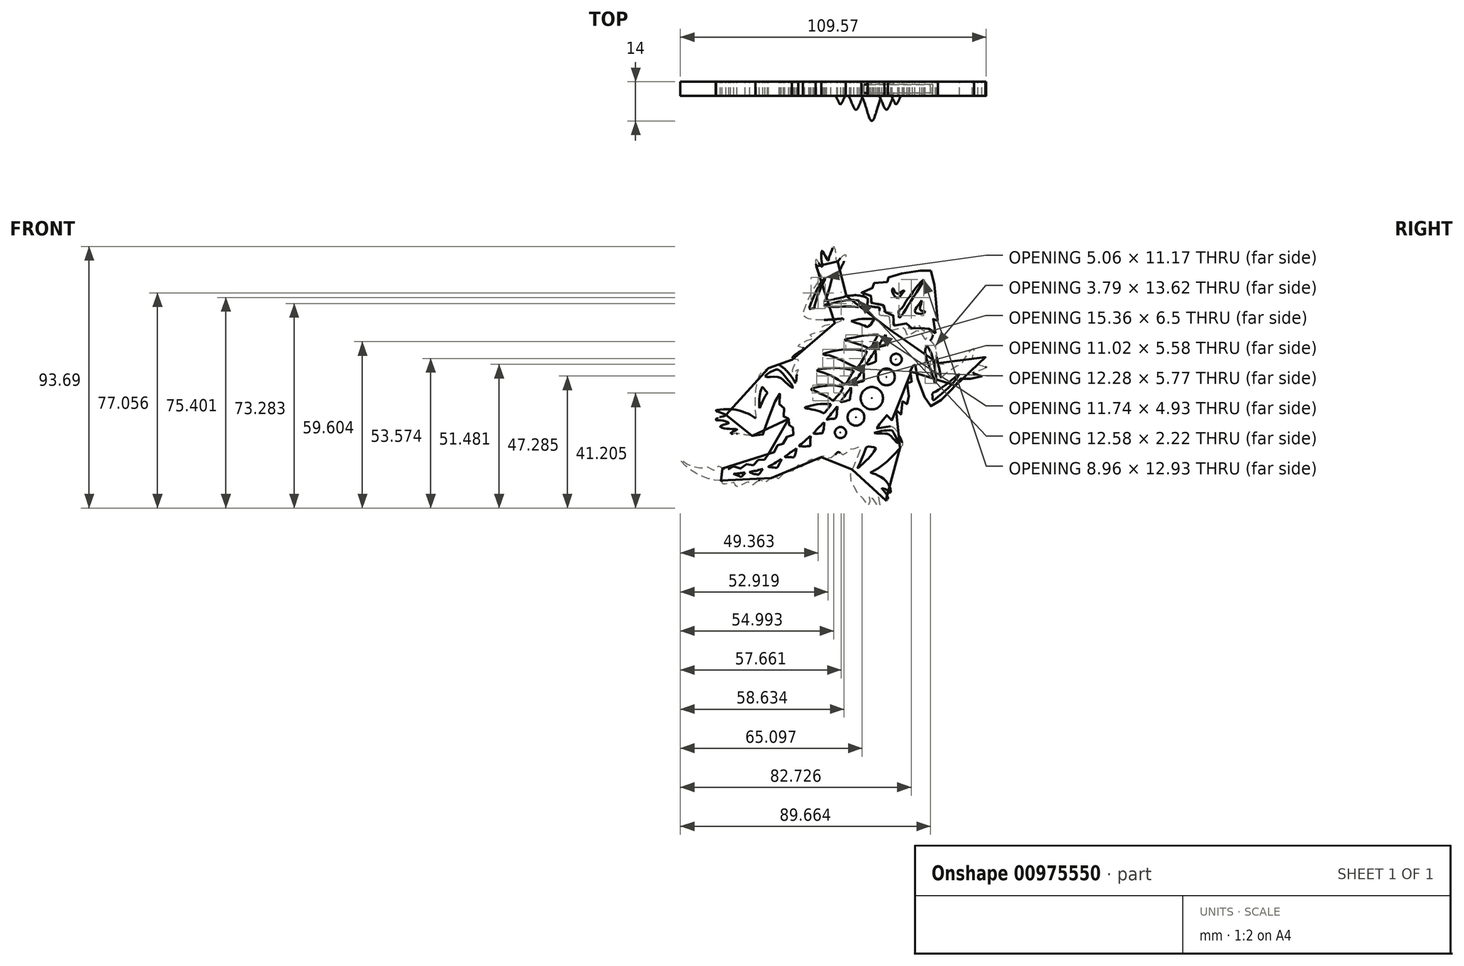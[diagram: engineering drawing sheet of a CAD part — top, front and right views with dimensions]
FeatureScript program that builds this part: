
annotation { "Feature Type Name" : "Feature", "Feature Type Description" : "" }
export const myFeature = defineFeature(function(context is Context, id is Id, definition is map)
    precondition{}
    {
        {
            var Q0;
            Q0=qCreatedBy(makeId("Front.planeOp"),FACE);
            var sketch = newSketch(context, id + "F0", { "sketchPlane" : qUnion([Q0])});
            skFitSpline(sketch, "E0", {"points": [v(30.98, 38.07) * mm, v(31.77, 36.1) * mm, v(32.57, 30.36) * mm, v(33.16, 24.69) * mm, v(33.49, 20.2) * mm, v(32.73, 21.01) * mm, v(31.9, 21.39) * mm, v(32.1, 19.86) * mm, v(32.63, 16.77) * mm, v(32.17, 14.46) * mm, v(30.12, 17.43) * mm, v(29.13, 16.1) * mm, v(27.08, 18.28) * mm, v(26.59, 18.68) * mm, v(24.12, 17.21) * mm, v(23.4, 17.05) * mm, v(22.34, 19.03) * mm, v(21.8, 19.22) * mm, v(18.26, 18.5) * mm, v(17.54, 18.54) * mm, v(17.59, 20.46) * mm, v(17.38, 22.76) * mm, v(16.26, 23.16) * mm, v(14.34, 23.28) * mm, v(13.92, 23.44) * mm, v(14, 25.28) * mm, v(14.04, 25.87) * mm, v(10.42, 26.54) * mm, v(9.56, 26.64) * mm, v(9.6, 27.95) * mm, v(9.65, 28.97) * mm, v(7.14, 29.74) * mm, v(6.18, 29.96) * mm, v(7.76, 31.22) * mm, v(10.13, 31.88) * mm, v(8.42, 32.8) * mm, v(12.25, 33.84) * mm, v(15.61, 33.83) * mm, v(14.75, 34.36) * mm, v(14.38, 34.8) * mm, v(15.66, 35.53) * mm, v(17.25, 36.18) * mm, v(21.91, 37.35) * mm, v(27.53, 38.14) * mm, v(29.94, 38.54) * mm, v(30.98, 38.07) * mm]});
            skFitSpline(sketch, "E1", {"points": [v(19.45, 29.85) * mm, v(20.35, 30.4) * mm, v(21.46, 30.98) * mm, v(21.33, 30.6) * mm, v(20.9, 30.12) * mm, v(20.16, 29.02) * mm, v(19.1, 28.32) * mm, v(17.88, 29.2) * mm, v(17.25, 30.44) * mm, v(17.21, 31.24) * mm, v(17.48, 31.8) * mm, v(18.04, 30.71) * mm, v(18.74, 30) * mm, v(19.45, 29.85) * mm]});
            skFitSpline(sketch, "E2", {"points": [v(27.77, 27.41) * mm, v(27.7, 26.6) * mm, v(27.26, 25.37) * mm, v(27.1, 24.63) * mm, v(27.46, 23.88) * mm, v(28.57, 23.55) * mm, v(29, 23.37) * mm, v(28.56, 22.98) * mm, v(27.22, 22.63) * mm, v(25.83, 22.88) * mm, v(25.3, 23.53) * mm, v(25.85, 24.77) * mm, v(26.88, 26.2) * mm, v(27.77, 27.41) * mm]});
            skFitSpline(sketch, "E3", {"points": [v(28.5, 34.9) * mm, v(27.24, 32.43) * mm, v(24.96, 28.8) * mm, v(22.63, 25.34) * mm, v(21.6, 23.47) * mm, v(19.69, 21.14) * mm, v(19.69, 21.84) * mm, v(19.55, 22.77) * mm, v(19.5, 23.7) * mm, v(20.2, 24.22) * mm, v(21.04, 25.06) * mm, v(22.35, 27.49) * mm, v(23.6, 28.93) * mm, v(25.66, 31.92) * mm, v(26.6, 33) * mm, v(28.5, 34.9) * mm]});
            skFitSpline(sketch, "E4", {"points": [v(16.5, 16.87) * mm, v(17.44, 16.9) * mm, v(19.63, 17.39) * mm, v(21.31, 17.57) * mm, v(21.73, 16.94) * mm, v(22.25, 15.64) * mm, v(22.65, 15.04) * mm, v(23.64, 15.34) * mm, v(25.2, 16.21) * mm, v(26.14, 16.7) * mm, v(27.05, 16.05) * mm, v(27.92, 15.1) * mm, v(29.16, 13.48) * mm, v(29.47, 13.82) * mm, v(29.68, 14.15) * mm, v(31.3, 12.65) * mm, v(32.54, 10.76) * mm, v(33.07, 7.62) * mm, v(34.14, 2.7) * mm, v(34.44, 1.05) * mm, v(34.67, -0.18) * mm, v(35.23, 0.28) * mm, v(37.82, 2.37) * mm, v(41.03, 4.33) * mm, v(42.2, 4.96) * mm, v(43.62, 7.27) * mm, v(45.23, 9.43) * mm, v(46.45, 10.27) * mm, v(46.36, 9.2) * mm, v(45.96, 7.32) * mm, v(45.9, 6.76) * mm, v(46.93, 6.79) * mm, v(49.42, 7.22) * mm, v(50.64, 7.17) * mm, v(49.98, 6.44) * mm, v(48.25, 4.94) * mm, v(47.94, 4.51) * mm, v(48.93, 4.14) * mm, v(50.4, 3.72) * mm, v(50.87, 3.45) * mm, v(50, 2.95) * mm, v(47.3, 1.94) * mm, v(46.17, 1.56) * mm, v(47.02, 0.9) * mm, v(48.32, 0.6) * mm, v(49.36, 0.36) * mm, v(48.17, -0.1) * mm, v(46.03, -0.55) * mm, v(43.33, -0.33) * mm, v(42.29, 0) * mm, v(41.05, -1.68) * mm, v(39.24, -3.71) * mm, v(37.77, -5.41) * mm, v(34.31, -8.57) * mm, v(32, -10.1) * mm, v(30.95, -10.46) * mm, v(30.18, -9.62) * mm, v(28.92, -7.54) * mm, v(26.88, -2.44) * mm, v(25.89, 1.9) * mm, v(25.53, 4.16) * mm, v(25.14, 5.87) * mm, v(24.76, 4.77) * mm, v(24.57, 3) * mm, v(24.43, 1.89) * mm, v(23.98, 1.99) * mm, v(23.57, 2.03) * mm, v(23.65, 0.51) * mm, v(24.26, -1.7) * mm, v(24.38, -2.48) * mm, v(23.4, -2.45) * mm, v(22.61, -2.2) * mm, v(22.81, -3.5) * mm, v(23.2, -6.77) * mm, v(23.03, -8.7) * mm, v(22.76, -9.87) * mm, v(21.97, -8.68) * mm, v(21.18, -7.7) * mm, v(20.87, -8.99) * mm, v(20.93, -12) * mm, v(20.24, -13.48) * mm, v(19.96, -12.95) * mm, v(19.3, -12.16) * mm, v(18.57, -11.86) * mm, v(18.16, -12.83) * mm, v(17.48, -14.78) * mm, v(16.44, -16.05) * mm, v(15.77, -14.7) * mm, v(15.1, -13.65) * mm, v(14.5, -14.81) * mm, v(12.16, -17.32) * mm, v(10.55, -18.8) * mm, v(12.04, -18.33) * mm, v(15.24, -17.64) * mm, v(17.09, -17.77) * mm, v(18.99, -19.58) * mm, v(20.75, -23.41) * mm, v(20.85, -24.4) * mm, v(20, -25.45) * mm, v(14.98, -30.6) * mm, v(10.06, -33.87) * mm, v(9.44, -34.18) * mm, v(10.65, -34.66) * mm, v(12.9, -35.72) * mm, v(15.33, -37.73) * mm, v(16.72, -41.13) * mm, v(16.33, -41.49) * mm, v(15.77, -40.83) * mm, v(14.51, -40.07) * mm, v(13.52, -39.97) * mm, v(14.42, -41) * mm, v(15.8, -43.9) * mm, v(15.6, -44.69) * mm, v(13.88, -43.39) * mm, v(12.04, -42.44) * mm, v(12.48, -43.66) * mm, v(12.6, -46.96) * mm, v(11.45, -45.04) * mm, v(9.7, -43.16) * mm, v(8.82, -42.66) * mm, v(9.18, -44.52) * mm, v(8.89, -46.16) * mm, v(7.23, -44.1) * mm, v(4.52, -41.27) * mm, v(3.77, -39.58) * mm, v(2.33, -36.78) * mm, v(2.47, -34.03) * mm, v(3.74, -31.4) * mm, v(5.4, -27.1) * mm, v(5.99, -24.9) * mm, v(4.46, -25.43) * mm, v(3.02, -25.88) * mm, v(2, -25.88) * mm, v(1.33, -26.57) * mm, v(0.39, -27.54) * mm, v(-0.3, -27.93) * mm, v(-0.97, -27.54) * mm, v(-1.4, -27.22) * mm, v(-2.22, -26.93) * mm, v(-2.86, -27.46) * mm, v(-4.16, -28.57) * mm, v(-5.27, -29.29) * mm, v(-5.74, -29.12) * mm, v(-7.05, -28.34) * mm, v(-7.44, -28.18) * mm, v(-7.85, -28.37) * mm, v(-8.75, -29.4) * mm, v(-9.9, -30.31) * mm, v(-10.92, -30.12) * mm, v(-11.7, -29.46) * mm, v(-12.41, -29.68) * mm, v(-13.91, -31.23) * mm, v(-15.24, -32.29) * mm, v(-15.82, -31.89) * mm, v(-16.39, -31.45) * mm, v(-17.07, -32.14) * mm, v(-18.07, -33.14) * mm, v(-18.98, -34.04) * mm, v(-19.86, -33.87) * mm, v(-20.43, -33.53) * mm, v(-20.98, -33.96) * mm, v(-22.94, -35.83) * mm, v(-23.74, -36.46) * mm, v(-24.5, -35.84) * mm, v(-25.2, -35.46) * mm, v(-26, -36.06) * mm, v(-27.49, -37.3) * mm, v(-28.49, -37.93) * mm, v(-29.28, -37.34) * mm, v(-30.04, -36.8) * mm, v(-30.67, -37.14) * mm, v(-32.41, -38.4) * mm, v(-33, -38.77) * mm, v(-33.79, -38.38) * mm, v(-34.38, -37.56) * mm, v(-35.69, -38.16) * mm, v(-37.04, -38.77) * mm, v(-38.12, -39.18) * mm, v(-38.51, -39.22) * mm, v(-39.06, -38.5) * mm, v(-39.47, -37.79) * mm, v(-40.26, -37.95) * mm, v(-42.5, -38.32) * mm, v(-43.46, -38.32) * mm, v(-43.73, -37.83) * mm, v(-43.77, -37.24) * mm, v(-44.5, -37.14) * mm, v(-48.09, -36.56) * mm, v(-52.7, -34.73) * mm, v(-57.15, -31.6) * mm, v(-58.7, -29.6) * mm, v(-58.46, -29.53) * mm, v(-57.52, -30.3) * mm, v(-54.63, -31.96) * mm, v(-50.26, -32.51) * mm, v(-48.9, -32.2) * mm, v(-48.05, -32.73) * mm, v(-46.6, -33.45) * mm, v(-45.76, -32.68) * mm, v(-44.89, -31.8) * mm, v(-43.99, -32.45) * mm, v(-42.6, -33.47) * mm, v(-42.18, -33.6) * mm, v(-41.75, -33.16) * mm, v(-40.79, -32.1) * mm, v(-40.36, -31.79) * mm, v(-39.69, -32.04) * mm, v(-38.19, -32.9) * mm, v(-37.47, -33.08) * mm, v(-36.55, -31.96) * mm, v(-35.75, -30.96) * mm, v(-34.8, -31.34) * mm, v(-33.89, -31.76) * mm, v(-32.92, -31.82) * mm, v(-32.03, -30.6) * mm, v(-31.34, -29.68) * mm, v(-30.62, -29.82) * mm, v(-29.4, -30.04) * mm, v(-28.73, -29.96) * mm, v(-28.45, -28.76) * mm, v(-27.9, -27.52) * mm, v(-26.93, -27.57) * mm, v(-25.73, -27.66) * mm, v(-25.18, -27.52) * mm, v(-25.01, -26.07) * mm, v(-24.62, -24.69) * mm, v(-23.85, -24.5) * mm, v(-22.9, -24.55) * mm, v(-22.12, -24.47) * mm, v(-21.8, -23.36) * mm, v(-21.35, -21.58) * mm, v(-20.46, -21.47) * mm, v(-19.38, -21.47) * mm, v(-18.6, -21.28) * mm, v(-18, -19.67) * mm, v(-17.8, -18.33) * mm, v(-18.38, -18.18) * mm, v(-19.27, -18.09) * mm, v(-19.83, -17.95) * mm, v(-19.69, -17.11) * mm, v(-19.35, -15.67) * mm, v(-19.38, -15.17) * mm, v(-20.35, -14.98) * mm, v(-21.1, -14.84) * mm, v(-21.68, -14.53) * mm, v(-21.68, -13.92) * mm, v(-21.55, -12.29) * mm, v(-21.55, -11.23) * mm, v(-22.57, -10.87) * mm, v(-23.29, -10.48) * mm, v(-23.13, -9.24) * mm, v(-22.93, -6.74) * mm, v(-23.18, -5.93) * mm, v(-23.88, -7.07) * mm, v(-25.46, -10.26) * mm, v(-28.1, -17.95) * mm, v(-29.17, -20.64) * mm, v(-30.53, -21.1) * mm, v(-34.08, -20.91) * mm, v(-37.52, -20.39) * mm, v(-39.58, -20.28) * mm, v(-40.71, -20.33) * mm, v(-40.21, -19.72) * mm, v(-38.41, -18.86) * mm, v(-40.5, -18.61) * mm, v(-42.93, -18.36) * mm, v(-44.4, -17.78) * mm, v(-42.6, -16.92) * mm, v(-41.38, -16.48) * mm, v(-42.9, -15.75) * mm, v(-44.8, -15.53) * mm, v(-46.04, -15.34) * mm, v(-44.7, -14.45) * mm, v(-42.32, -13.67) * mm, v(-43.82, -12.93) * mm, v(-45.96, -12.04) * mm, v(-43.77, -11.62) * mm, v(-39.1, -11.65) * mm, v(-35.27, -12.81) * mm, v(-32.95, -13.98) * mm, v(-31.53, -14.73) * mm, v(-31.64, -13.12) * mm, v(-31.75, -5.82) * mm, v(-31.06, -1.52) * mm, v(-29.81, 1.42) * mm, v(-27.34, 3.08) * mm, v(-24.68, 4.22) * mm, v(-23.54, 4.41) * mm, v(-22.6, 3.91) * mm, v(-20.9, 2.47) * mm, v(-18.3, -0.78) * mm, v(-17.35, -2.22) * mm, v(-17.13, -0.55) * mm, v(-16.94, 1.03) * mm, v(-16.6, 2.05) * mm, v(-16.39, 2.55) * mm, v(-17.2, 2.33) * mm, v(-18.24, 1.33) * mm, v(-18.55, 2.41) * mm, v(-16.91, 5.38) * mm, v(-16.33, 6) * mm, v(-17.41, 6.38) * mm, v(-18.72, 6.24) * mm, v(-18.41, 7.16) * mm, v(-14.75, 9.71) * mm, v(-14.22, 10.07) * mm, v(-15.5, 10.68) * mm, v(-16.44, 10.88) * mm, v(-16.33, 11.37) * mm, v(-12.72, 13.26) * mm, v(-10.9, 14.01) * mm, v(-12.25, 14.95) * mm, v(-11.5, 15.56) * mm, v(-7.25, 16.64) * mm, v(-6.25, 16.93) * mm, v(-7.03, 17.42) * mm, v(-7.95, 17.86) * mm, v(-7.14, 18.47) * mm, v(-4.31, 19.09) * mm, v(-1.26, 20.03) * mm, v(-0.28, 20.78) * mm, v(-3.37, 20.7) * mm, v(-8.72, 20.45) * mm, v(-13.16, 21.02) * mm, v(-14.72, 22.18) * mm, v(-14.7, 22.87) * mm, v(-12.69, 28.19) * mm, v(-9.95, 33.1) * mm, v(-8.59, 35.01) * mm, v(-8.04, 35.9) * mm, v(-8.79, 37.12) * mm, v(-10.03, 40.04) * mm, v(-10.05, 42.13) * mm, v(-9.52, 41.44) * mm, v(-8.65, 40.1) * mm, v(-7.92, 39.44) * mm, v(-8.04, 40.74) * mm, v(-8.17, 43.93) * mm, v(-7.93, 45.21) * mm, v(-7.3, 44.32) * mm, v(-6.1, 42.23) * mm, v(-5.73, 41.72) * mm, v(-5.35, 43.02) * mm, v(-4.43, 45.35) * mm, v(-3.77, 46.73) * mm, v(-3.19, 44.98) * mm, v(-2.94, 42.57) * mm, v(-2.73, 41.17) * mm, v(-1.66, 42.18) * mm, v(-0.53, 43.3) * mm, v(0.46, 43.83) * mm, v(0.26, 42.21) * mm, v(-1.1, 39.24) * mm, v(-1.74, 37.99) * mm, v(-3.04, 37.11) * mm, v(-3.61, 36.43) * mm, v(-4, 36.11) * mm, v(-5.05, 32.78) * mm, v(-5.88, 29.82) * mm, v(-6.6, 28.1) * mm, v(-6.9, 27.3) * mm, v(-4.27, 27.65) * mm, v(-1.21, 28.4) * mm, v(1.4, 29.03) * mm, v(4.06, 29.28) * mm, v(6.25, 29.05) * mm, v(8.3, 28.16) * mm, v(8.42, 27.2) * mm, v(8.33, 26.32) * mm, v(8.38, 25.62) * mm, v(9.17, 25.32) * mm, v(11.57, 25.01) * mm, v(12.65, 24.71) * mm, v(12.62, 23.9) * mm, v(12.5, 23.08) * mm, v(12.58, 22.36) * mm, v(13.81, 22.05) * mm, v(15.16, 21.96) * mm, v(15.97, 21.77) * mm, v(16.18, 20.72) * mm, v(16.43, 18.08) * mm, v(16.5, 16.87) * mm]});
            skFitSpline(sketch, "E5", {"points": [v(-6.8, 35.68) * mm, v(-7.08, 34.54) * mm, v(-7.83, 33.13) * mm, v(-8.5, 31.52) * mm, v(-9.41, 29.47) * mm, v(-10.08, 27.36) * mm, v(-10.6, 25.25) * mm, v(-10.66, 24.59) * mm, v(-11.3, 24.64) * mm, v(-12.52, 24.3) * mm, v(-12.22, 25.7) * mm, v(-11.3, 28.03) * mm, v(-10.38, 29.88) * mm, v(-9.52, 31.72) * mm, v(-8.44, 33.63) * mm, v(-7.42, 34.99) * mm, v(-6.8, 35.68) * mm]});
            skFitSpline(sketch, "E6", {"points": [v(-7.33, 25.74) * mm, v(-5.84, 26.06) * mm, v(-3.31, 26.64) * mm, v(-0.9, 27.14) * mm, v(2.13, 27.53) * mm, v(4.68, 27.42) * mm, v(5.32, 27.25) * mm, v(5.43, 26.67) * mm, v(5.2, 25.72) * mm, v(5.07, 25.03) * mm, v(4.12, 25.17) * mm, v(1.65, 25.28) * mm, v(-1.04, 25.2) * mm, v(-3.4, 25.14) * mm, v(-5.8, 25.3) * mm, v(-7.37, 25.53) * mm, v(-7.33, 25.74) * mm]});
            skFitSpline(sketch, "E7", {"points": [v(2.52, 20.01) * mm, v(3.64, 20.33) * mm, v(5.33, 20.66) * mm, v(7.42, 20.86) * mm, v(8.76, 20.86) * mm, v(9.82, 20.86) * mm, v(10.27, 20.68) * mm, v(10.7, 20.46) * mm, v(10.39, 20.05) * mm, v(9.94, 19.4) * mm, v(9.45, 18.7) * mm, v(8.66, 18.07) * mm, v(8.35, 17.87) * mm, v(7.82, 18.15) * mm, v(6.9, 18.5) * mm, v(5.33, 19.07) * mm, v(3.91, 19.56) * mm, v(3, 19.84) * mm, v(2.52, 20.01) * mm]});
            skFitSpline(sketch, "E8", {"points": [v(12.27, 15.1) * mm, v(11.97, 14.74) * mm, v(11.52, 14.05) * mm, v(11.05, 13.17) * mm, v(10.72, 12.5) * mm, v(10.37, 11.87) * mm, v(9.86, 11) * mm, v(9.37, 10.32) * mm, v(9.1, 10.05) * mm, v(8.76, 10.24) * mm, v(8.1, 10.6) * mm, v(6.9, 11.09) * mm, v(5.48, 11.64) * mm, v(3.64, 12.24) * mm, v(1.72, 12.77) * mm, v(0.38, 13.05) * mm, v(0.17, 13.17) * mm, v(0.2, 13.36) * mm, v(0.72, 13.54) * mm, v(1.95, 13.85) * mm, v(3.54, 14.17) * mm, v(5.48, 14.58) * mm, v(7.6, 14.87) * mm, v(9.23, 15.03) * mm, v(10.97, 15.1) * mm, v(11.76, 15.13) * mm, v(12.27, 15.1) * mm]});
            skFitSpline(sketch, "E9", {"points": [v(14.82, 15.13) * mm, v(14.9, 14.74) * mm, v(14.9, 13.64) * mm, v(14.92, 12.26) * mm, v(14.94, 11.54) * mm, v(14.54, 11.36) * mm, v(13.74, 11.07) * mm, v(12.88, 10.83) * mm, v(12.33, 10.75) * mm, v(11.95, 10.73) * mm, v(12.19, 11.1) * mm, v(12.97, 12.28) * mm, v(13.66, 13.46) * mm, v(14.37, 14.5) * mm, v(14.82, 15.13) * mm]});
            skFitSpline(sketch, "E10", {"points": [v(11.13, 9.6) * mm, v(11.23, 9.05) * mm, v(11.3, 8.18) * mm, v(11.33, 7.18) * mm, v(11.39, 6.22) * mm, v(11.35, 5.58) * mm, v(10.84, 5.36) * mm, v(9.54, 4.83) * mm, v(8.52, 4.6) * mm, v(8.01, 4.65) * mm, v(8.19, 5.1) * mm, v(8.76, 6.03) * mm, v(9.54, 7.1) * mm, v(10.19, 8.15) * mm, v(10.76, 9.03) * mm, v(11.13, 9.6) * mm]});
            skFitSpline(sketch, "E11", {"points": [v(29.64, 11.33) * mm, v(30.02, 10.8) * mm, v(30.63, 9.75) * mm, v(31.3, 8.2) * mm, v(31.88, 5.98) * mm, v(32.24, 4.23) * mm, v(32.52, 2.81) * mm, v(32.8, 1.01) * mm, v(32.94, -0.54) * mm, v(32.83, -1.76) * mm, v(32.83, -2.23) * mm, v(32.63, -2.26) * mm, v(32.24, -1.1) * mm, v(31.6, 0.62) * mm, v(31.08, 2.32) * mm, v(30.47, 3.98) * mm, v(29.91, 5.4) * mm, v(29.36, 6.86) * mm, v(29.05, 8.36) * mm, v(29.05, 10) * mm, v(29.5, 11.07) * mm, v(29.64, 11.33) * mm]});
            skFitSpline(sketch, "E12", {"points": [v(41.26, 0.96) * mm, v(40.95, 0.5) * mm, v(40.27, -0.5) * mm, v(38.7, -2.45) * mm, v(36.74, -4.38) * mm, v(34.78, -6.18) * mm, v(32.7, -7.9) * mm, v(32.04, -8.38) * mm, v(31.7, -8.15) * mm, v(31.71, -7.58) * mm, v(31.66, -6.6) * mm, v(31.6, -5.82) * mm, v(32.3, -5.5) * mm, v(33.35, -4.95) * mm, v(35.3, -3.58) * mm, v(37.22, -2.16) * mm, v(38.8, -0.82) * mm, v(40.37, 0.37) * mm, v(41.26, 0.96) * mm]});
            skFitSpline(sketch, "E13", {"points": [v(-7.75, 8.27) * mm, v(-6.98, 8.53) * mm, v(-5, 9.09) * mm, v(-2.64, 9.56) * mm, v(-0.63, 9.81) * mm, v(1.5, 9.86) * mm, v(3.5, 9.84) * mm, v(5.6, 9.58) * mm, v(7.74, 9.16) * mm, v(8.23, 9) * mm, v(7.93, 8.48) * mm, v(7.2, 7.08) * mm, v(6.23, 5.45) * mm, v(5.3, 4.17) * mm, v(4.8, 3.56) * mm, v(4.5, 3.33) * mm, v(3.68, 3.65) * mm, v(1.98, 4.5) * mm, v(0.7, 5.15) * mm, v(-0.8, 5.92) * mm, v(-2.08, 6.55) * mm, v(-3.64, 7.13) * mm, v(-5, 7.62) * mm, v(-6.46, 7.88) * mm, v(-7.4, 8.04) * mm, v(-7.75, 8.27) * mm]});
            skFitSpline(sketch, "E14", {"points": [v(-9.85, 2.28) * mm, v(-9.4, 2.6) * mm, v(-8.35, 2.88) * mm, v(-6.7, 3.07) * mm, v(-4.71, 3.19) * mm, v(-2.73, 3.23) * mm, v(-0.7, 3.12) * mm, v(1.05, 2.9) * mm, v(2.52, 2.58) * mm, v(3.5, 2.23) * mm, v(3.12, 1.65) * mm, v(2.4, 0.5) * mm, v(1.75, -0.7) * mm, v(0.88, -1.94) * mm, v(0.28, -2.62) * mm, v(-0.24, -2.34) * mm, v(-1.2, -1.55) * mm, v(-2.5, -0.73) * mm, v(-4.25, 0.3) * mm, v(-5.72, 0.92) * mm, v(-7.19, 1.41) * mm, v(-8.6, 1.86) * mm, v(-9.85, 2.28) * mm]});
            skFitSpline(sketch, "E15", {"points": [v(6.83, 2.8) * mm, v(6.93, 1.97) * mm, v(7.07, 0.7) * mm, v(7.07, -0.5) * mm, v(7.02, -1.36) * mm, v(6.37, -1.6) * mm, v(5.01, -2) * mm, v(3.5, -2.22) * mm, v(3.64, -1.9) * mm, v(4.34, -0.85) * mm, v(5.27, 0.43) * mm, v(6.04, 1.6) * mm, v(6.62, 2.42) * mm, v(6.83, 2.8) * mm]});
            skFitSpline(sketch, "E16", {"points": [v(2.34, -3.68) * mm, v(2.44, -4.39) * mm, v(2.42, -5.35) * mm, v(2.28, -6.47) * mm, v(2, -7.8) * mm, v(1.99, -8.2) * mm, v(1.28, -8.37) * mm, v(0.34, -8.74) * mm, v(-0.62, -8.92) * mm, v(-1.27, -8.92) * mm, v(-1, -8.37) * mm, v(-0.23, -7.3) * mm, v(0.63, -6.17) * mm, v(1.65, -4.82) * mm, v(2.16, -4.02) * mm, v(2.34, -3.68) * mm]});
            skFitSpline(sketch, "E17", {"points": [v(-0.27, -3.8) * mm, v(-0.84, -4.68) * mm, v(-1.27, -5.55) * mm, v(-2.43, -6.8) * mm, v(-3.37, -7.94) * mm, v(-3.86, -8.55) * mm, v(-4.94, -7.82) * mm, v(-6.53, -6.86) * mm, v(-8.08, -6.16) * mm, v(-9.76, -5.33) * mm, v(-11.08, -4.78) * mm, v(-11.82, -4.6) * mm, v(-11.86, -4.45) * mm, v(-10.9, -3.9) * mm, v(-9.16, -3.5) * mm, v(-7.15, -3.21) * mm, v(-5.36, -2.95) * mm, v(-2.8, -3.05) * mm, v(-0.92, -3.45) * mm, v(-0.27, -3.8) * mm]});
            skFitSpline(sketch, "E18", {"points": [v(-2.45, -10.54) * mm, v(-2.39, -11.13) * mm, v(-2.5, -11.62) * mm, v(-2.67, -12.55) * mm, v(-2.67, -13.39) * mm, v(-2.73, -14.1) * mm, v(-3, -14.7) * mm, v(-3.62, -14.94) * mm, v(-4.53, -14.99) * mm, v(-5.27, -15.09) * mm, v(-5.75, -15.2) * mm, v(-6.26, -15.25) * mm, v(-5.8, -14.58) * mm, v(-5.16, -13.84) * mm, v(-4.37, -12.8) * mm, v(-3.77, -12.04) * mm, v(-2.82, -10.93) * mm, v(-2.45, -10.54) * mm]});
            skFitSpline(sketch, "E19", {"points": [v(-4.78, -9.63) * mm, v(-5.1, -10.42) * mm, v(-5.75, -11.34) * mm, v(-6.58, -12.33) * mm, v(-7.04, -12.75) * mm, v(-7.37, -13.01) * mm, v(-7.98, -12.65) * mm, v(-8.77, -12.33) * mm, v(-9.86, -11.99) * mm, v(-10.98, -11.74) * mm, v(-11.97, -11.56) * mm, v(-13.14, -11.38) * mm, v(-13.92, -11.2) * mm, v(-14.13, -10.95) * mm, v(-13.62, -10.75) * mm, v(-12.43, -10.4) * mm, v(-11, -10) * mm, v(-9.27, -9.73) * mm, v(-7.63, -9.66) * mm, v(-6.08, -9.6) * mm, v(-5.34, -9.6) * mm, v(-4.78, -9.63) * mm]});
            skFitSpline(sketch, "E20", {"points": [v(-7.23, -16.22) * mm, v(-7.2, -17.13) * mm, v(-7.37, -18.71) * mm, v(-7.64, -19.74) * mm, v(-7.75, -20.13) * mm, v(-8.61, -20.24) * mm, v(-9.84, -20.38) * mm, v(-10.75, -20.24) * mm, v(-11.08, -20.24) * mm, v(-10.61, -19.74) * mm, v(-9.78, -18.8) * mm, v(-8.7, -17.69) * mm, v(-7.78, -16.74) * mm, v(-7.23, -16.22) * mm]});
            skFitSpline(sketch, "E21", {"points": [v(-12.03, -21.16) * mm, v(-12.03, -21.68) * mm, v(-12.1, -22.65) * mm, v(-12.08, -23.51) * mm, v(-12.14, -24.26) * mm, v(-12.22, -24.7) * mm, v(-12.86, -24.79) * mm, v(-14.27, -24.87) * mm, v(-15.19, -24.84) * mm, v(-16.16, -24.7) * mm, v(-15.52, -24.15) * mm, v(-14.44, -23.24) * mm, v(-13.47, -22.26) * mm, v(-12.64, -21.6) * mm, v(-12.03, -21.16) * mm]});
            skFitSpline(sketch, "E22", {"points": [v(-17.12, -25.58) * mm, v(-17.2, -26.14) * mm, v(-17.35, -26.85) * mm, v(-17.52, -27.64) * mm, v(-17.87, -28.53) * mm, v(-18.01, -28.76) * mm, v(-18.74, -28.75) * mm, v(-19.63, -28.67) * mm, v(-20.34, -28.65) * mm, v(-21.28, -28.6) * mm, v(-20.77, -28.14) * mm, v(-20.06, -27.63) * mm, v(-19.23, -27.02) * mm, v(-18.46, -26.49) * mm, v(-17.5, -25.86) * mm, v(-17.12, -25.58) * mm]});
            skFitSpline(sketch, "E23", {"points": [v(-22.53, -29.42) * mm, v(-22.68, -29.99) * mm, v(-23.03, -30.71) * mm, v(-23.47, -31.59) * mm, v(-23.87, -32.36) * mm, v(-24.41, -32.48) * mm, v(-25.58, -32.36) * mm, v(-26.38, -32.31) * mm, v(-26.94, -32.25) * mm, v(-27.18, -32.16) * mm, v(-26.72, -31.9) * mm, v(-25.93, -31.45) * mm, v(-25.22, -31.04) * mm, v(-24.2, -30.4) * mm, v(-23.2, -29.75) * mm, v(-22.53, -29.42) * mm]});
            skFitSpline(sketch, "E24", {"points": [v(-29.16, -32.95) * mm, v(-29.4, -33.27) * mm, v(-29.8, -33.93) * mm, v(-30.27, -34.44) * mm, v(-30.78, -34.97) * mm, v(-31.2, -34.95) * mm, v(-31.94, -34.82) * mm, v(-32.51, -34.65) * mm, v(-33.3, -34.34) * mm, v(-33.67, -34.2) * mm, v(-33.88, -34.04) * mm, v(-33.55, -33.94) * mm, v(-32.6, -33.76) * mm, v(-31.56, -33.58) * mm, v(-30.62, -33.32) * mm, v(-29.36, -33.04) * mm, v(-29.16, -32.95) * mm]});
            skFitSpline(sketch, "E25", {"points": [v(-35.5, -34.27) * mm, v(-35.76, -34.6) * mm, v(-36.14, -35.1) * mm, v(-36.5, -35.45) * mm, v(-36.93, -35.77) * mm, v(-37.4, -35.6) * mm, v(-38.09, -35.3) * mm, v(-38.81, -35.1) * mm, v(-39.28, -34.88) * mm, v(-39.59, -34.72) * mm, v(-38.9, -34.65) * mm, v(-38, -34.52) * mm, v(-36.9, -34.42) * mm, v(-36.14, -34.3) * mm, v(-35.5, -34.27) * mm]});
            skFitSpline(sketch, "E26", {"points": [v(-28.45, 0.31) * mm, v(-27.23, 1.3) * mm, v(-25.85, 2.06) * mm, v(-24.57, 2.53) * mm, v(-24.13, 2.72) * mm, v(-23.18, 2.36) * mm, v(-22.38, 1.59) * mm, v(-21.38, 0.53) * mm, v(-20.55, -0.55) * mm, v(-19.58, -1.71) * mm, v(-18.69, -3.1) * mm, v(-18.3, -3.93) * mm, v(-18.72, -3.71) * mm, v(-19.63, -3.16) * mm, v(-21.13, -1.85) * mm, v(-21.94, -1.08) * mm, v(-22.74, -0.41) * mm, v(-24.4, 0.12) * mm, v(-26.43, -0.02) * mm, v(-27.6, 0) * mm, v(-28.45, 0.31) * mm]});
            skFitSpline(sketch, "E27", {"points": [v(-30.34, -11.17) * mm, v(-30.48, -9.57) * mm, v(-30.4, -7.7) * mm, v(-30.2, -6.24) * mm, v(-29.87, -4.74) * mm, v(-29.5, -3.9) * mm, v(-29.34, -3.55) * mm, v(-28.84, -4.1) * mm, v(-28.2, -4.85) * mm, v(-27.54, -5.6) * mm, v(-27.79, -6.1) * mm, v(-28.73, -7.6) * mm, v(-29.31, -8.87) * mm, v(-29.9, -10.1) * mm, v(-30.34, -11.17) * mm]});
            skFitSpline(sketch, "E28", {"points": [v(10.77, -20.12) * mm, v(11.72, -19.7) * mm, v(12.85, -19.4) * mm, v(14.21, -19.18) * mm, v(15.63, -19.13) * mm, v(16.9, -19.1) * mm, v(17.54, -19.76) * mm, v(18.18, -20.82) * mm, v(18.76, -22.18) * mm, v(19.15, -23.67) * mm, v(18.62, -23.29) * mm, v(17.93, -22.5) * mm, v(17.15, -21.57) * mm, v(16.3, -20.79) * mm, v(15.43, -20.37) * mm, v(14.63, -20.26) * mm, v(12.69, -20.18) * mm, v(11.63, -20.18) * mm, v(10.77, -20.12) * mm]});
            skFitSpline(sketch, "E29", {"points": [v(7.94, -25.09) * mm, v(9, -24.95) * mm, v(10.02, -25) * mm, v(11.33, -25.45) * mm, v(11.05, -26.12) * mm, v(10.55, -26.9) * mm, v(9.64, -28.09) * mm, v(8.5, -29.33) * mm, v(7.39, -30.36) * mm, v(6.56, -31.2) * mm, v(5.67, -31.94) * mm, v(4.8, -32.7) * mm, v(5.12, -32.05) * mm, v(5.86, -30.36) * mm, v(6.53, -28.83) * mm, v(7.03, -27.5) * mm, v(7.61, -25.87) * mm, v(7.94, -25.09) * mm]});
            skSolve(sketch);
        }
        {
            var Q0;
            Q0=makeQuery(id+"F0.imprint","IMPRINT",FACE,{"disambiguationData":[TD([[makeQuery(id+"F0.imprint","IMPRINT",EDGE,{"derivedFrom":sQuery(id+"F0.wireOp",EDGE,"E4")}),-1.0]])]});
            var Q1;
            Q1=makeQuery(id+"F0.imprint","IMPRINT",FACE,{"disambiguationData":[TD([[makeQuery(id+"F0.imprint","IMPRINT",EDGE,{"derivedFrom":sQuery(id+"F0.wireOp",EDGE,"E0")}),-1.0]])]});
            extrude(context, id + "F1", {"entities" : qUnion([Q0, Q1]), "endBound" : BoundingType.SYMMETRIC, "depth" : 5 * mm, "offsetDistance" : 25 * mm});
        }
        {
            var Q0;
            Q0=qCreatedBy(makeId("Front.planeOp"),FACE);
            var sketch = newSketch(context, id + "F2", { "sketchPlane" : qUnion([Q0])});
            skFitSpline(sketch, "E30", {"points": [v(7.8, 30.36) * mm, v(11.01, 29.86) * mm, v(14.57, 27.91) * mm, v(18.17, 24.25) * mm, v(18.73, 20.55) * mm, v(18.76, 19.8) * mm, v(20.9, 20.46) * mm, v(24.93, 20.39) * mm, v(29.78, 19.07) * mm, v(31.83, 16.33) * mm, v(29.78, 12.24) * mm, v(20.64, 14.23) * mm, v(15.6, 15.74) * mm, v(12.87, 20.31) * mm, v(9.58, 22.98) * mm, v(6.77, 25.9) * mm, v(6.52, 27.98) * mm, v(7.8, 30.36) * mm]});
            skSolve(sketch);
        }
        {
            var Q0;
            Q0 = qSketchRegion(id + "F2", true);
            extrude(context, id + "F3", {"entities" : qUnion([Q0]), "operationType" : NewBodyOperationType.ADD, "endBound" : BoundingType.SYMMETRIC, "depth" : 3 * mm, "offsetDistance" : 25 * mm});
        }
        {
            var Q0;
            Q0=makeQuery(id+"F1.opExtrude","CAP_FACE",FACE,{"disambiguationData":[OSD([sQuery(id+"F0.wireOp",EDGE,"E4"),sQuery(id+"F0.wireOp",EDGE,"E5"),sQuery(id+"F0.wireOp",EDGE,"E6"),sQuery(id+"F0.wireOp",EDGE,"E7"),sQuery(id+"F0.wireOp",EDGE,"E8"),sQuery(id+"F0.wireOp",EDGE,"E9"),sQuery(id+"F0.wireOp",EDGE,"E10"),sQuery(id+"F0.wireOp",EDGE,"E11"),sQuery(id+"F0.wireOp",EDGE,"E12"),sQuery(id+"F0.wireOp",EDGE,"E13"),sQuery(id+"F0.wireOp",EDGE,"E14"),sQuery(id+"F0.wireOp",EDGE,"E15"),sQuery(id+"F0.wireOp",EDGE,"E16"),sQuery(id+"F0.wireOp",EDGE,"E17"),sQuery(id+"F0.wireOp",EDGE,"E18"),sQuery(id+"F0.wireOp",EDGE,"E19"),sQuery(id+"F0.wireOp",EDGE,"E20"),sQuery(id+"F0.wireOp",EDGE,"E21"),sQuery(id+"F0.wireOp",EDGE,"E22"),sQuery(id+"F0.wireOp",EDGE,"E23"),sQuery(id+"F0.wireOp",EDGE,"E24"),sQuery(id+"F0.wireOp",EDGE,"E25"),sQuery(id+"F0.wireOp",EDGE,"E26"),sQuery(id+"F0.wireOp",EDGE,"E27"),sQuery(id+"F0.wireOp",EDGE,"E28"),sQuery(id+"F0.wireOp",EDGE,"E29")])],"isStart":false});
            var sketch = newSketch(context, id + "F4", { "sketchPlane" : qUnion([Q0])});
            skCircle(sketch, "E31", {"center": v(18.62, 6.33) * mm, "radius": 2 * mm});
            skCircle(sketch, "E32", {"center": v(15.16, 0) * mm, "radius": 3 * mm});
            skCircle(sketch, "E33", {"center": v(9.9, -7.6) * mm, "radius": 4 * mm});
            skCircle(sketch, "E34", {"center": v(4.21, -14.42) * mm, "radius": 3 * mm});
            skCircle(sketch, "E35", {"center": v(-1.33, -19.9) * mm, "radius": 2 * mm});
            skSolve(sketch);
        }
        {
            var Q0;
            Q0=makeQuery(id+"F4.imprint","IMPRINT",FACE,{"disambiguationData":[TD([[makeQuery(id+"F4.imprint","IMPRINT",EDGE,{"derivedFrom":makeQuery(id+"F1.opExtrude","CAP_EDGE",EDGE,{"disambiguationData":[OSD([sQuery(id+"F0.wireOp",EDGE,"E4")])],"isStart":false})}),-1.0]])]});
            cPlane(context, id + "F5", {"entities" : qUnion([Q0]), "cplaneType" : CPlaneType.OFFSET, "offset" : 9 * mm, "width" : 150 * mm, "height" : 150 * mm});
        }
        {
            var Q0;
            Q0=makeQuery(id+"F4.imprint","IMPRINT",FACE,{"disambiguationData":[TD([[makeQuery(id+"F4.imprint","IMPRINT",EDGE,{"derivedFrom":makeQuery(id+"F1.opExtrude","CAP_EDGE",EDGE,{"disambiguationData":[OSD([sQuery(id+"F0.wireOp",EDGE,"E4")])],"isStart":false})}),-1.0]])]});
            cPlane(context, id + "F6", {"entities" : qUnion([Q0]), "cplaneType" : CPlaneType.OFFSET, "offset" : 5 * mm, "width" : 150 * mm, "height" : 150 * mm});
        }
        {
            var Q0;
            Q0=makeQuery(id+"F4.imprint","IMPRINT",FACE,{"disambiguationData":[TD([[makeQuery(id+"F4.imprint","IMPRINT",EDGE,{"derivedFrom":makeQuery(id+"F1.opExtrude","CAP_EDGE",EDGE,{"disambiguationData":[OSD([sQuery(id+"F0.wireOp",EDGE,"E4")])],"isStart":false})}),-1.0]])]});
            cPlane(context, id + "F7", {"entities" : qUnion([Q0]), "cplaneType" : CPlaneType.OFFSET, "offset" : 3 * mm, "width" : 150 * mm, "height" : 150 * mm});
        }
        {
            var Q0;
            Q0=qCreatedBy(id+"F5.planeOp",FACE);
            var sketch = newSketch(context, id + "F8", { "sketchPlane" : qUnion([Q0])});
            skCircle(sketch, "E36", {"center": v(9.9, -7.62) * mm, "radius": 0 * mm});
            skSolve(sketch);
        }
        {
            var Q0;
            Q0=qCreatedBy(id+"F6.planeOp",FACE);
            var sketch = newSketch(context, id + "F9", { "sketchPlane" : qUnion([Q0])});
            skCircle(sketch, "E37", {"center": v(15.15, 0) * mm, "radius": 0 * mm});
            skCircle(sketch, "E38", {"center": v(4.2, -14.42) * mm, "radius": 0 * mm});
            skSolve(sketch);
        }
        {
            var Q0;
            Q0=qCreatedBy(id+"F7.planeOp",FACE);
            var sketch = newSketch(context, id + "F10", { "sketchPlane" : qUnion([Q0])});
            skCircle(sketch, "E39", {"center": v(18.6, 6.3) * mm, "radius": 0 * mm});
            skCircle(sketch, "E40", {"center": v(-1.35, -19.92) * mm, "radius": 0 * mm});
            skSolve(sketch);
        }
        {
            var Q1;
            Q1=makeQuery(id+"F4.imprint","IMPRINT",FACE,{"disambiguationData":[TD([[makeQuery(id+"F4.imprint","IMPRINT",EDGE,{"derivedFrom":sQuery(id+"F4.wireOp",EDGE,"E33")}),1.0]])]});
            var Q2;
            Q2=makeQuery(id+"F8.imprint","IMPRINT",FACE,{"disambiguationData":[TD([[makeQuery(id+"F8.imprint","IMPRINT",EDGE,{"derivedFrom":sQuery(id+"F8.wireOp",EDGE,"E36")}),1.0]])]});
            loft(context, id + "F11", {"operationType" : NewBodyOperationType.ADD, "startCondition" : LoftEndDerivativeType.TANGENT_TO_PROFILE, "startMagnitude" : 1, "endCondition" : LoftEndDerivativeType.TANGENT_TO_PROFILE, "endMagnitude" : 1, "sheetProfilesArray" : [{ "sheetProfileEntities" : qUnion([Q1]) }, { "sheetProfileEntities" : qUnion([Q2]) }]});
        }
        {
            var Q1;
            Q1=makeQuery(id+"F4.imprint","IMPRINT",FACE,{"disambiguationData":[TD([[makeQuery(id+"F4.imprint","IMPRINT",EDGE,{"derivedFrom":sQuery(id+"F4.wireOp",EDGE,"E31")}),1.0]])]});
            var Q2;
            Q2=makeQuery(id+"F10.imprint","IMPRINT",FACE,{"disambiguationData":[TD([[makeQuery(id+"F10.imprint","IMPRINT",EDGE,{"derivedFrom":sQuery(id+"F10.wireOp",EDGE,"E39")}),1.0]])]});
            loft(context, id + "F12", {"operationType" : NewBodyOperationType.ADD, "startCondition" : LoftEndDerivativeType.TANGENT_TO_PROFILE, "startMagnitude" : 1, "endCondition" : LoftEndDerivativeType.TANGENT_TO_PROFILE, "endMagnitude" : 1, "sheetProfilesArray" : [{ "sheetProfileEntities" : qUnion([Q1]) }, { "sheetProfileEntities" : qUnion([Q2]) }]});
        }
        {
            var Q1;
            Q1=makeQuery(id+"F4.imprint","IMPRINT",FACE,{"disambiguationData":[TD([[makeQuery(id+"F4.imprint","IMPRINT",EDGE,{"derivedFrom":sQuery(id+"F4.wireOp",EDGE,"E32")}),1.0]])]});
            var Q2;
            Q2=makeQuery(id+"F9.imprint","IMPRINT",FACE,{"disambiguationData":[TD([[makeQuery(id+"F9.imprint","IMPRINT",EDGE,{"derivedFrom":sQuery(id+"F9.wireOp",EDGE,"E37")}),1.0]])]});
            loft(context, id + "F13", {"operationType" : NewBodyOperationType.ADD, "startCondition" : LoftEndDerivativeType.TANGENT_TO_PROFILE, "startMagnitude" : 1, "endCondition" : LoftEndDerivativeType.TANGENT_TO_PROFILE, "endMagnitude" : 1, "sheetProfilesArray" : [{ "sheetProfileEntities" : qUnion([Q1]) }, { "sheetProfileEntities" : qUnion([Q2]) }]});
        }
        {
            var Q1;
            Q1=makeQuery(id+"F4.imprint","IMPRINT",FACE,{"disambiguationData":[TD([[makeQuery(id+"F4.imprint","IMPRINT",EDGE,{"derivedFrom":sQuery(id+"F4.wireOp",EDGE,"E34")}),1.0]])]});
            var Q2;
            Q2=makeQuery(id+"F9.imprint","IMPRINT",FACE,{"disambiguationData":[TD([[makeQuery(id+"F9.imprint","IMPRINT",EDGE,{"derivedFrom":sQuery(id+"F9.wireOp",EDGE,"E38")}),1.0]])]});
            loft(context, id + "F14", {"operationType" : NewBodyOperationType.ADD, "startCondition" : LoftEndDerivativeType.TANGENT_TO_PROFILE, "startMagnitude" : 1, "endCondition" : LoftEndDerivativeType.TANGENT_TO_PROFILE, "endMagnitude" : 1, "sheetProfilesArray" : [{ "sheetProfileEntities" : qUnion([Q1]) }, { "sheetProfileEntities" : qUnion([Q2]) }]});
        }
        {
            var Q1;
            Q1=makeQuery(id+"F4.imprint","IMPRINT",FACE,{"disambiguationData":[TD([[makeQuery(id+"F4.imprint","IMPRINT",EDGE,{"derivedFrom":sQuery(id+"F4.wireOp",EDGE,"E35")}),1.0]])]});
            var Q2;
            Q2=makeQuery(id+"F10.imprint","IMPRINT",FACE,{"disambiguationData":[TD([[makeQuery(id+"F10.imprint","IMPRINT",EDGE,{"derivedFrom":sQuery(id+"F10.wireOp",EDGE,"E40")}),1.0]])]});
            loft(context, id + "F15", {"operationType" : NewBodyOperationType.ADD, "startCondition" : LoftEndDerivativeType.TANGENT_TO_PROFILE, "startMagnitude" : 1, "endCondition" : LoftEndDerivativeType.TANGENT_TO_PROFILE, "endMagnitude" : 1, "sheetProfilesArray" : [{ "sheetProfileEntities" : qUnion([Q1]) }, { "sheetProfileEntities" : qUnion([Q2]) }]});
        }
    });
